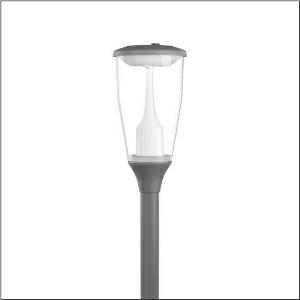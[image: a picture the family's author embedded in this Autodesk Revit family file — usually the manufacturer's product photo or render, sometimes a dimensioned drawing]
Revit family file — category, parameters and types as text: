
# Revit family: dl_11_iq___st1_2a_5xa5565ev14hp00022_f5ed
name_source: partatom
category: Lighting Fixtures
units: mm (PartAtom-declared; Revit-internal decimal feet)

## family parameters
Cut with Voids When Loaded = No
Host = Face
Light Source = No
Part Type = Normal
Room Calculation Point = No
Round Connector Dimension = Use Diameter
Shared = No

## types (1)
- --- (1 x LED, 4790 lm, 33.5 W, 3000K)
    Apparent Load = 34 VA
    CIE Flux Codes = 23 60 93 95 100
    Color Rendering = 70
    Color Temperature = 3000K
    Default Elevation = 1800 mm
    Description = DL 11 iQ, mast luminaire, Module 540 iQ-SR, primary light control with 3 zone facetted reflector, of plastic, silver coated, highly specular, structured, primary optical cover: cover, of PMMA, transparent, light distribution: ST1.2a, light emission: direct distribution, primary light characteristic: asymmetric, installation type: post-top, LED, High Power LED, rated luminous flux: 4.790lm, luminous efficacy: 143lm/W, light colour: 730, colour temperature: 3000K, control gear: iQ-Street Remote, D4i with power reduction, control: pre-setting: logarithmic dimming characteristic, Street-Remote, Auto-Match, Temp-Guard, Lumen-Switch, Night-Set, Smart-Wire, Light-Fading, Desk-Remote (wireless, voltage-free reading and setting of iQ features in the workshop via application-optimized NFC function/RFID function), optimised constant luminous flux control (CLO 2.0), mains connection: 220..240V, AC, 50/60Hz, connection cable pre-assembled, cable length: 5,5m, start of lifetime: 34W, end of service life: 36W, reduction: 15W, luminaire housing, upper part, of diecast aluminium, coated, Siteco® metallic grey (DB 702S), spigot size: 60mm (post-top), mounting height: 3..5m, post-top mast mounting element, of diecast aluminium, coated, Siteco® metallic grey (DB 702S), Module 540 iQ-SR, traffic white (RAL 9016), equipment: Power, Smart Interface above, protection rating (complete): IP66, insulation class (complete): insulation class II (safety insulation), certification: CE, ENEC, ENEC+, VDE, impact resistance: IK07, packaging unit: 1 piece

Light Distribution: ST1.2a
    Height = 665 mm
    Lamp = 1 x LED
    Lamp Light Flux = 4790 lm
    Lamp Power = 33.5 W
    Lamp count = 1
    Length = 334 mm
    Luminous efficacy = 143 lm/W
    Manufacturer = Siteco
    ModVariant = No
    Model = 5XA5565EV14HP00022
    Number of Poles = 1
    OnlyDefault = Yes
    Power Factor = 1
    Product Name = DL 11 iQ | ST1.2a
    Product group = mast luminaire | pylon top
    ProductGroupID = 6100
    Protection Class = Protection class II
    Protection Degree = IP 66
    RLX_Detail_Level = 1
    RLX_Emergency_Light_Flux = 0 lm
    RLX_Emergency_Type = 0
    RLX_Emergency_Type_DB = No
    RlxData = <blob elided: 161785 chars, md5=5b5af482>
    Socket = socket
    Standby Power = 0 W
    System Light Flux = 4790 lm
    System Power = 34 W
    Type Comments = factory setting: luminous flux: 100 % | dim-lin: 254 | 695 mA
    Type Image = l_1337541.jpg
    URL = http://relux.com
    VarID = @adj_034006
    Voltage = 0 V
    Weight = 0.00 kg
    Width = 0 mm  [stored 0 ft]

note: [stored X ft] marks values corroborated as IEEE doubles in the binary element streams (Revit-internal decimal feet)

## geometry (parser evidence)
native form markers: Blend x4, Sweep x10
no freeform markers — native parametric forms only
